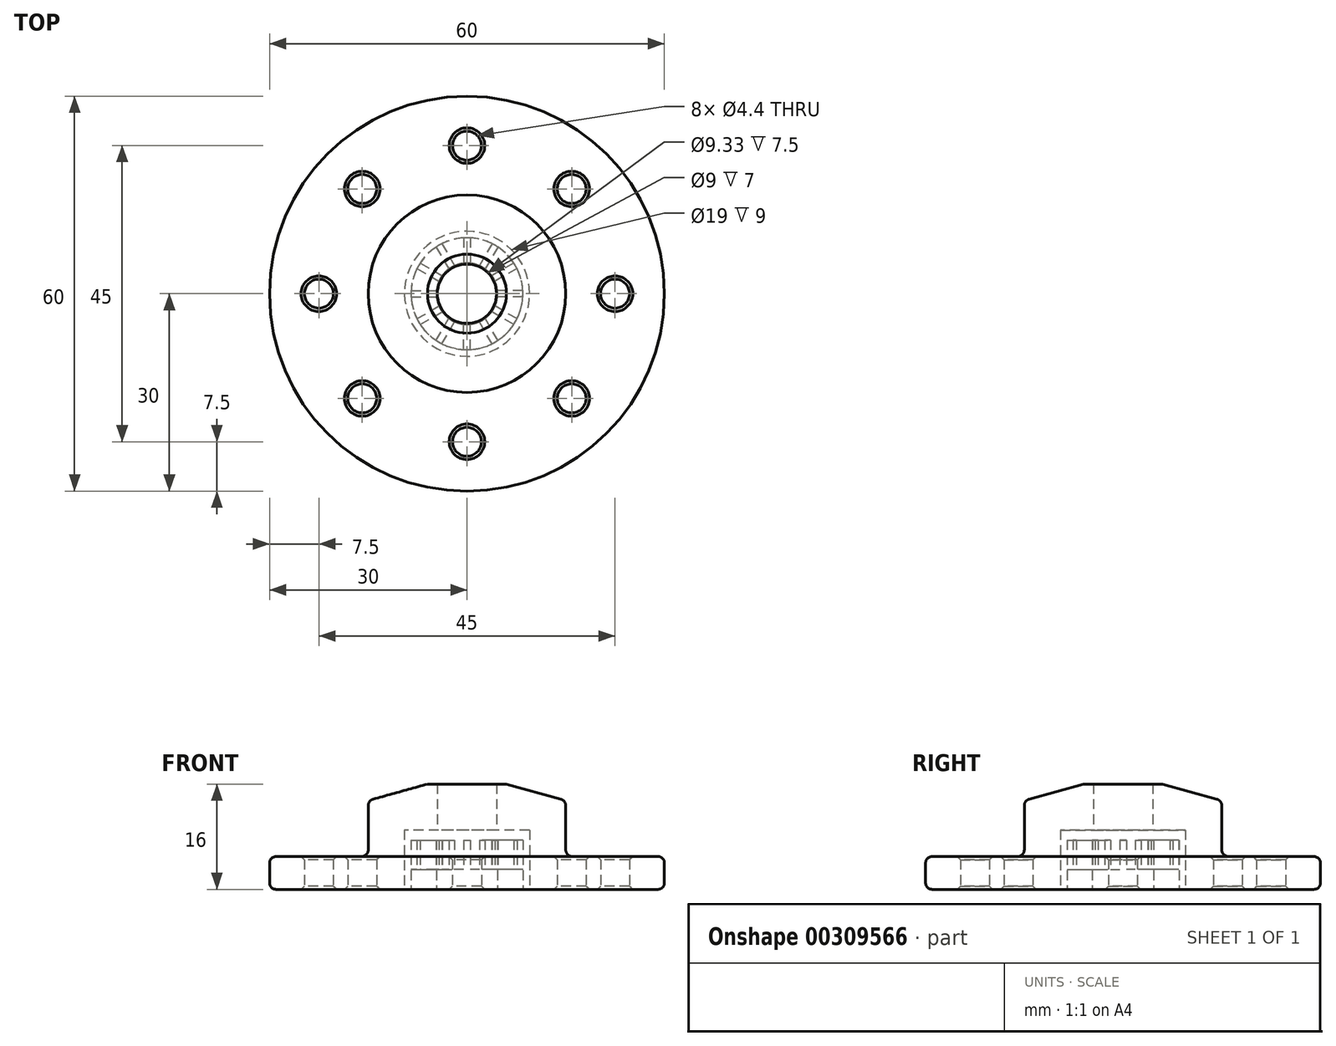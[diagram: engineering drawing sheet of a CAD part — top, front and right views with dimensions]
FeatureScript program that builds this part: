
annotation { "Feature Type Name" : "Feature", "Feature Type Description" : "" }
export const myFeature = defineFeature(function(context is Context, id is Id, definition is map)
    precondition{}
    {
        {
            var Q0;
            Q0=qCreatedBy(makeId("Top.planeOp"),FACE);
            var sketch = newSketch(context, id + "F0", { "sketchPlane" : qUnion([Q0])});
            skCircle(sketch, "E0", {"center": v(0, 0) * mm, "radius": 4.5 * mm});
            skCircle(sketch, "E1", {"center": v(0, 0) * mm, "radius": 6 * mm});
            skCircle(sketch, "E2", {"center": v(0, 0) * mm, "radius": 30 * mm});
            skCircle(sketch, "E3", {"center": v(0, 0) * mm, "radius": 9.5 * mm});
            skCircle(sketch, "E4", {"center": v(0, 0) * mm, "radius": 15 * mm});
            skLineSegment(sketch, "E5", {"start": v(15, 0) * mm, "end": v(30, 0) * mm});
            skCircle(sketch, "E6", {"center": v(22.5, 0) * mm, "radius": 2.2 * mm});
            skCircle(sketch, "E7.1.0", {"center": v(15.9, 15.9) * mm, "radius": 2.2 * mm});
            skCircle(sketch, "E7.2.0", {"center": v(0, 22.5) * mm, "radius": 2.2 * mm});
            skCircle(sketch, "E7.3.0", {"center": v(-15.9, 15.9) * mm, "radius": 2.2 * mm});
            skCircle(sketch, "E7.4.0", {"center": v(-22.5, 0) * mm, "radius": 2.2 * mm});
            skCircle(sketch, "E7.5.0", {"center": v(-15.9, -15.9) * mm, "radius": 2.2 * mm});
            skCircle(sketch, "E7.6.0", {"center": v(0, -22.5) * mm, "radius": 2.2 * mm});
            skCircle(sketch, "E7.7.0", {"center": v(15.9, -15.9) * mm, "radius": 2.2 * mm});
            skSolve(sketch);
        }
        {
            var Q0;
            Q0=makeQuery(id+"F0.imprint","IMPRINT",FACE,{"disambiguationData":[TD([[makeQuery(id+"F0.imprint","IMPRINT",EDGE,{"derivedFrom":sQuery(id+"F0.wireOp",EDGE,"E1")}),-1.0]])]});
            var Q1;
            Q1=makeQuery(id+"F0.imprint","IMPRINT",FACE,{"disambiguationData":[TD([[makeQuery(id+"F0.imprint","IMPRINT",EDGE,{"derivedFrom":sQuery(id+"F0.wireOp",EDGE,"E2")}),1.0]])]});
            var Q2;
            Q2=makeQuery(id+"F0.imprint","IMPRINT",FACE,{"disambiguationData":[TD([[makeQuery(id+"F0.imprint","IMPRINT",EDGE,{"derivedFrom":sQuery(id+"F0.wireOp",EDGE,"E3")}),-1.0]])]});
            extrude(context, id + "F1", {"entities" : qUnion([Q0, Q1, Q2]), "depth" : 5 * mm});
        }
        {
            var Q0;
            Q0=makeQuery(id+"F0.imprint","IMPRINT",FACE,{"disambiguationData":[TD([[makeQuery(id+"F0.imprint","IMPRINT",EDGE,{"derivedFrom":sQuery(id+"F0.wireOp",EDGE,"E0")}),-1.0]])]});
            extrude(context, id + "F2", {"entities" : qUnion([Q0]), "operationType" : NewBodyOperationType.ADD, "depth" : 16 * mm});
        }
        {
            var Q0;
            Q0=makeQuery(id+"F0.imprint","IMPRINT",FACE,{"disambiguationData":[TD([[makeQuery(id+"F0.imprint","IMPRINT",EDGE,{"derivedFrom":sQuery(id+"F0.wireOp",EDGE,"E3")}),-1.0]])]});
            var Q1;
            Q1=makeQuery(id+"F0.imprint","IMPRINT",FACE,{"disambiguationData":[TD([[makeQuery(id+"F0.imprint","IMPRINT",EDGE,{"derivedFrom":sQuery(id+"F0.wireOp",EDGE,"E1")}),-1.0]])]});
            extrude(context, id + "F3", {"entities" : qUnion([Q0, Q1]), "operationType" : NewBodyOperationType.ADD, "depth" : 13.5 * mm});
        }
        {
            var Q0;
            Q0=makeQuery(id+"F0.imprint","IMPRINT",FACE,{"disambiguationData":[TD([[makeQuery(id+"F0.imprint","IMPRINT",EDGE,{"derivedFrom":sQuery(id+"F0.wireOp",EDGE,"E0")}),-1.0]])]});
            var Q1;
            Q1=makeQuery(id+"F0.imprint","IMPRINT",FACE,{"disambiguationData":[TD([[makeQuery(id+"F0.imprint","IMPRINT",EDGE,{"derivedFrom":sQuery(id+"F0.wireOp",EDGE,"E1")}),-1.0]])]});
            extrude(context, id + "F4", {"entities" : qUnion([Q0, Q1]), "operationType" : NewBodyOperationType.REMOVE, "depth" : 9 * mm});
        }
        {
            var Q0;
            Q0=qCreatedBy(makeId("Front.planeOp"),FACE);
            var sketch = newSketch(context, id + "F5", { "sketchPlane" : qUnion([Q0])});
            skLineSegment(sketch, "E8", {"start": v(0, 0) * mm, "end": v(0, 16) * mm});
            skLineSegment(sketch, "E9", {"start": v(0, 16) * mm, "end": v(6, 16) * mm});
            skLineSegment(sketch, "E10", {"start": v(6, 16) * mm, "end": v(6, 13.5) * mm});
            skLineSegment(sketch, "E11", {"start": v(6, 13.5) * mm, "end": v(15, 13.5) * mm});
            skLineSegment(sketch, "E12", {"start": v(15, 13.5) * mm, "end": v(6, 16) * mm});
            skSolve(sketch);
        }
        {
            var Q0;
            Q0=makeQuery(id+"F5.imprint","IMPRINT",FACE,{"disambiguationData":[TD([[makeQuery(id+"F5.imprint","IMPRINT",EDGE,{"derivedFrom":sQuery(id+"F5.wireOp",EDGE,"E10")}),1.0]])]});
            var Q1;
            Q1=sQuery(id+"F5.wireOp",EDGE,"E8");
            revolve(context, id + "F6", {"operationType" : NewBodyOperationType.ADD, "entities" : qUnion([Q0]), "axis" : qUnion([Q1]), "revolveType" : RevolveType.FULL});
        }
        {
            var Q0;
            Q0=makeQuery(id+"F1.opExtrude","SWEPT_FACE",FACE,{"disambiguationData":[OSD([sQuery(id+"F0.wireOp",EDGE,"E2")])]});
            var Q1;
            Q1=makeQuery(id+"F3.opExtrude","SWEPT_FACE",FACE,{"disambiguationData":[OSD([sQuery(id+"F0.wireOp",EDGE,"E4")])]});
            var Q2;
            Q2=makeQuery(id+"F4.boolean.opBoolean","COPY",EDGE,{"derivedFrom":makeQuery(id+"F4.opExtrude","CAP_EDGE",EDGE,{"disambiguationData":[OSD([sQuery(id+"F0.wireOp",EDGE,"E3")])],"isStart":true})});
            fillet(context, id + "F7", {"entities" : qUnion([Q0, Q1, Q2]), "radius" : 1 * mm, "tangentPropagation" : true, "allowEdgeOverflow" : false});
        }
        {
            var Q0;
            Q0=makeQuery(id+"F1.opExtrude","SWEPT_FACE",FACE,{"disambiguationData":[OSD([sQuery(id+"F0.wireOp",EDGE,"E7.3.0")])]});
            var Q1;
            Q1=makeQuery(id+"F1.opExtrude","SWEPT_FACE",FACE,{"disambiguationData":[OSD([sQuery(id+"F0.wireOp",EDGE,"E7.2.0")])]});
            var Q2;
            Q2=makeQuery(id+"F1.opExtrude","SWEPT_FACE",FACE,{"disambiguationData":[OSD([sQuery(id+"F0.wireOp",EDGE,"E7.4.0")])]});
            var Q3;
            Q3=makeQuery(id+"F1.opExtrude","SWEPT_FACE",FACE,{"disambiguationData":[OSD([sQuery(id+"F0.wireOp",EDGE,"E7.5.0")])]});
            var Q4;
            Q4=makeQuery(id+"F1.opExtrude","SWEPT_FACE",FACE,{"disambiguationData":[OSD([sQuery(id+"F0.wireOp",EDGE,"E7.1.0")])]});
            var Q5;
            Q5=makeQuery(id+"F1.opExtrude","SWEPT_FACE",FACE,{"disambiguationData":[OSD([sQuery(id+"F0.wireOp",EDGE,"E7.6.0")])]});
            var Q6;
            Q6=makeQuery(id+"F1.opExtrude","SWEPT_FACE",FACE,{"disambiguationData":[OSD([sQuery(id+"F0.wireOp",EDGE,"E7.7.0")])]});
            var Q7;
            Q7=makeQuery(id+"F1.opExtrude","SWEPT_FACE",FACE,{"disambiguationData":[OSD([sQuery(id+"F0.wireOp",EDGE,"E6")])]});
            var Q8;
            Q8=makeQuery(id+"F4.boolean.opBoolean","COPY",EDGE,{"derivedFrom":makeQuery(id+"F4.opExtrude","CAP_EDGE",EDGE,{"disambiguationData":[OSD([sQuery(id+"F0.wireOp",EDGE,"E0")])],"isStart":false})});
            chamfer(context, id + "F8", {"entities" : qUnion([Q0, Q1, Q2, Q3, Q4, Q5, Q6, Q7, Q8]), "width" : 0.5 * mm, "tangentPropagation" : true});
        }
        {
            var Q0;
            {var subQ0=sQuery(id+"F0.wireOp",EDGE,"E1");Q0=makeQuery(id+"F2.boolean.opBoolean","MERGE",FACE,{"derivedFrom":[makeQuery(id+"F1.opExtrude","CAP_FACE",FACE,{"disambiguationData":[OSD([subQ0,sQuery(id+"F0.wireOp",EDGE,"E2"),sQuery(id+"F0.wireOp",EDGE,"E6"),sQuery(id+"F0.wireOp",EDGE,"E7.1.0"),sQuery(id+"F0.wireOp",EDGE,"E7.2.0"),sQuery(id+"F0.wireOp",EDGE,"E7.3.0"),sQuery(id+"F0.wireOp",EDGE,"E7.4.0"),sQuery(id+"F0.wireOp",EDGE,"E7.5.0"),sQuery(id+"F0.wireOp",EDGE,"E7.6.0"),sQuery(id+"F0.wireOp",EDGE,"E7.7.0")])],"isStart":true}),makeQuery(id+"F2.opExtrude","CAP_FACE",FACE,{"disambiguationData":[OSD([sQuery(id+"F0.wireOp",EDGE,"E0"),subQ0])],"isStart":true})]});}
            var sketch = newSketch(context, id + "F9", { "sketchPlane" : qUnion([Q0])});
            skCircle(sketch, "E13", {"center": v(0, 0) * mm, "radius": 4.67 * mm});
            skLineSegment(sketch, "E14", {"start": v(0, 0) * mm, "end": v(0, 4.5) * mm});
            skLineSegment(sketch, "E15", {"start": v(0, 4.5) * mm, "end": v(0, 8.5) * mm});
            skLineSegment(sketch, "E16.bottom", {"start": v(-0.5, 8.5) * mm, "end": v(0.5, 8.5) * mm});
            skLineSegment(sketch, "E16.top", {"start": v(-0.5, 4.5) * mm, "end": v(0.5, 4.5) * mm});
            skLineSegment(sketch, "E16.left", {"start": v(-0.5, 8.5) * mm, "end": v(-0.5, 4.5) * mm});
            skLineSegment(sketch, "E16.right", {"start": v(0.5, 8.5) * mm, "end": v(0.5, 4.5) * mm});
            skPoint(sketch, "E16.middle", {"position": v(0, 6.5) * mm});
            skCircle(sketch, "E17", {"center": v(0, 0) * mm, "radius": 8.5 * mm});
            skLineSegment(sketch, "E18.1.0", {"start": v(-3.82, 7.61) * mm, "end": v(-1.82, 4.15) * mm});
            skLineSegment(sketch, "E18.1.1", {"start": v(-4.68, 7.11) * mm, "end": v(-3.82, 7.61) * mm});
            skLineSegment(sketch, "E18.1.2", {"start": v(-4.68, 7.11) * mm, "end": v(-2.68, 3.65) * mm});
            skLineSegment(sketch, "E18.1.3", {"start": v(-2.68, 3.65) * mm, "end": v(-1.82, 4.15) * mm});
            skLineSegment(sketch, "E18.2.0", {"start": v(-7.11, 4.68) * mm, "end": v(-3.65, 2.68) * mm});
            skLineSegment(sketch, "E18.2.1", {"start": v(-7.61, 3.82) * mm, "end": v(-7.11, 4.68) * mm});
            skLineSegment(sketch, "E18.2.2", {"start": v(-7.61, 3.82) * mm, "end": v(-4.15, 1.82) * mm});
            skLineSegment(sketch, "E18.2.3", {"start": v(-4.15, 1.82) * mm, "end": v(-3.65, 2.68) * mm});
            skLineSegment(sketch, "E18.3.0", {"start": v(-8.5, 0.5) * mm, "end": v(-4.5, 0.5) * mm});
            skLineSegment(sketch, "E18.3.1", {"start": v(-8.5, -0.5) * mm, "end": v(-8.5, 0.5) * mm});
            skLineSegment(sketch, "E18.3.2", {"start": v(-8.5, -0.5) * mm, "end": v(-4.5, -0.5) * mm});
            skLineSegment(sketch, "E18.3.3", {"start": v(-4.5, -0.5) * mm, "end": v(-4.5, 0.5) * mm});
            skLineSegment(sketch, "E18.4.0", {"start": v(-7.61, -3.82) * mm, "end": v(-4.15, -1.82) * mm});
            skLineSegment(sketch, "E18.4.1", {"start": v(-7.11, -4.68) * mm, "end": v(-7.61, -3.82) * mm});
            skLineSegment(sketch, "E18.4.2", {"start": v(-7.11, -4.68) * mm, "end": v(-3.65, -2.68) * mm});
            skLineSegment(sketch, "E18.4.3", {"start": v(-3.65, -2.68) * mm, "end": v(-4.15, -1.82) * mm});
            skLineSegment(sketch, "E18.5.0", {"start": v(-4.68, -7.11) * mm, "end": v(-2.68, -3.65) * mm});
            skLineSegment(sketch, "E18.5.1", {"start": v(-3.82, -7.61) * mm, "end": v(-4.68, -7.11) * mm});
            skLineSegment(sketch, "E18.5.2", {"start": v(-3.82, -7.61) * mm, "end": v(-1.82, -4.15) * mm});
            skLineSegment(sketch, "E18.5.3", {"start": v(-1.82, -4.15) * mm, "end": v(-2.68, -3.65) * mm});
            skLineSegment(sketch, "E18.6.0", {"start": v(-0.5, -8.5) * mm, "end": v(-0.5, -4.5) * mm});
            skLineSegment(sketch, "E18.6.1", {"start": v(0.5, -8.5) * mm, "end": v(-0.5, -8.5) * mm});
            skLineSegment(sketch, "E18.6.2", {"start": v(0.5, -8.5) * mm, "end": v(0.5, -4.5) * mm});
            skLineSegment(sketch, "E18.6.3", {"start": v(0.5, -4.5) * mm, "end": v(-0.5, -4.5) * mm});
            skLineSegment(sketch, "E18.7.0", {"start": v(3.82, -7.61) * mm, "end": v(1.82, -4.15) * mm});
            skLineSegment(sketch, "E18.7.1", {"start": v(4.68, -7.11) * mm, "end": v(3.82, -7.61) * mm});
            skLineSegment(sketch, "E18.7.2", {"start": v(4.68, -7.11) * mm, "end": v(2.68, -3.65) * mm});
            skLineSegment(sketch, "E18.7.3", {"start": v(2.68, -3.65) * mm, "end": v(1.82, -4.15) * mm});
            skLineSegment(sketch, "E18.8.0", {"start": v(7.11, -4.68) * mm, "end": v(3.65, -2.68) * mm});
            skLineSegment(sketch, "E18.8.1", {"start": v(7.61, -3.82) * mm, "end": v(7.11, -4.68) * mm});
            skLineSegment(sketch, "E18.8.2", {"start": v(7.61, -3.82) * mm, "end": v(4.15, -1.82) * mm});
            skLineSegment(sketch, "E18.8.3", {"start": v(4.15, -1.82) * mm, "end": v(3.65, -2.68) * mm});
            skLineSegment(sketch, "E18.9.0", {"start": v(8.5, -0.5) * mm, "end": v(4.5, -0.5) * mm});
            skLineSegment(sketch, "E18.9.1", {"start": v(8.5, 0.5) * mm, "end": v(8.5, -0.5) * mm});
            skLineSegment(sketch, "E18.9.2", {"start": v(8.5, 0.5) * mm, "end": v(4.5, 0.5) * mm});
            skLineSegment(sketch, "E18.9.3", {"start": v(4.5, 0.5) * mm, "end": v(4.5, -0.5) * mm});
            skLineSegment(sketch, "E18.10.0", {"start": v(7.61, 3.82) * mm, "end": v(4.15, 1.82) * mm});
            skLineSegment(sketch, "E18.10.1", {"start": v(7.11, 4.68) * mm, "end": v(7.61, 3.82) * mm});
            skLineSegment(sketch, "E18.10.2", {"start": v(7.11, 4.68) * mm, "end": v(3.65, 2.68) * mm});
            skLineSegment(sketch, "E18.10.3", {"start": v(3.65, 2.68) * mm, "end": v(4.15, 1.82) * mm});
            skLineSegment(sketch, "E18.11.0", {"start": v(4.68, 7.11) * mm, "end": v(2.68, 3.65) * mm});
            skLineSegment(sketch, "E18.11.1", {"start": v(3.82, 7.61) * mm, "end": v(4.68, 7.11) * mm});
            skLineSegment(sketch, "E18.11.2", {"start": v(3.82, 7.61) * mm, "end": v(1.82, 4.15) * mm});
            skLineSegment(sketch, "E18.11.3", {"start": v(1.82, 4.15) * mm, "end": v(2.68, 3.65) * mm});
            skSolve(sketch);
        }
        {
            var Q0;
            {var subQ0=sQuery(id+"F9.wireOp",EDGE,"E18.10.2");var subQ1=sQuery(id+"F9.wireOp",EDGE,"E13");var subQ2=makeQuery(id+"F9.imprint","INTERSECT",VERTEX,{"derivedFrom":[subQ1,subQ0]});Q0=makeQuery(id+"F9.imprint","IMPRINT",FACE,{"disambiguationData":[TD([[makeQuery(id+"F9.imprint","IMPRINT",EDGE,{"disambiguationData":[TD([[subQ2,-1.0]])],"derivedFrom":subQ1}),-1.0]])]});}
            var Q1;
            {var subQ0=sQuery(id+"F9.wireOp",EDGE,"E18.11.0");var subQ1=sQuery(id+"F9.wireOp",EDGE,"E13");var subQ2=makeQuery(id+"F9.imprint","INTERSECT",VERTEX,{"derivedFrom":[subQ1,subQ0]});Q1=makeQuery(id+"F9.imprint","IMPRINT",FACE,{"disambiguationData":[TD([[makeQuery(id+"F9.imprint","IMPRINT",EDGE,{"disambiguationData":[TD([[subQ2,-1.0]])],"derivedFrom":subQ1}),-1.0]])]});}
            var Q2;
            {var subQ0=sQuery(id+"F9.wireOp",EDGE,"E18.11.2");var subQ1=sQuery(id+"F9.wireOp",EDGE,"E13");var subQ2=makeQuery(id+"F9.imprint","INTERSECT",VERTEX,{"derivedFrom":[subQ1,subQ0]});Q2=makeQuery(id+"F9.imprint","IMPRINT",FACE,{"disambiguationData":[TD([[makeQuery(id+"F9.imprint","IMPRINT",EDGE,{"disambiguationData":[TD([[subQ2,-1.0]])],"derivedFrom":subQ1}),-1.0]])]});}
            var Q3;
            {var subQ0=sQuery(id+"F9.wireOp",EDGE,"E16.right");var subQ1=sQuery(id+"F9.wireOp",EDGE,"E13");var subQ2=makeQuery(id+"F9.imprint","INTERSECT",VERTEX,{"derivedFrom":[subQ1,subQ0]});Q3=makeQuery(id+"F9.imprint","IMPRINT",FACE,{"disambiguationData":[TD([[makeQuery(id+"F9.imprint","IMPRINT",EDGE,{"disambiguationData":[TD([[subQ2,-1.0]])],"derivedFrom":subQ1}),-1.0]])]});}
            var Q4;
            {var subQ0=sQuery(id+"F9.wireOp",EDGE,"E15");var subQ1=sQuery(id+"F9.wireOp",EDGE,"E13");var subQ2=makeQuery(id+"F9.imprint","INTERSECT",VERTEX,{"derivedFrom":[subQ1,subQ0]});Q4=makeQuery(id+"F9.imprint","IMPRINT",FACE,{"disambiguationData":[TD([[makeQuery(id+"F9.imprint","IMPRINT",EDGE,{"disambiguationData":[TD([[subQ2,-1.0]])],"derivedFrom":subQ1}),-1.0]])]});}
            var Q5;
            {var subQ0=sQuery(id+"F9.wireOp",EDGE,"E16.left");var subQ1=sQuery(id+"F9.wireOp",EDGE,"E13");var subQ2=makeQuery(id+"F9.imprint","INTERSECT",VERTEX,{"derivedFrom":[subQ1,subQ0]});Q5=makeQuery(id+"F9.imprint","IMPRINT",FACE,{"disambiguationData":[TD([[makeQuery(id+"F9.imprint","IMPRINT",EDGE,{"disambiguationData":[TD([[subQ2,-1.0]])],"derivedFrom":subQ1}),-1.0]])]});}
            var Q6;
            {var subQ0=sQuery(id+"F9.wireOp",EDGE,"E18.1.0");var subQ1=sQuery(id+"F9.wireOp",EDGE,"E13");var subQ2=makeQuery(id+"F9.imprint","INTERSECT",VERTEX,{"derivedFrom":[subQ1,subQ0]});Q6=makeQuery(id+"F9.imprint","IMPRINT",FACE,{"disambiguationData":[TD([[makeQuery(id+"F9.imprint","IMPRINT",EDGE,{"disambiguationData":[TD([[subQ2,-1.0]])],"derivedFrom":subQ1}),-1.0]])]});}
            var Q7;
            {var subQ0=sQuery(id+"F9.wireOp",EDGE,"E18.1.2");var subQ1=sQuery(id+"F9.wireOp",EDGE,"E13");var subQ2=makeQuery(id+"F9.imprint","INTERSECT",VERTEX,{"derivedFrom":[subQ1,subQ0]});Q7=makeQuery(id+"F9.imprint","IMPRINT",FACE,{"disambiguationData":[TD([[makeQuery(id+"F9.imprint","IMPRINT",EDGE,{"disambiguationData":[TD([[subQ2,-1.0]])],"derivedFrom":subQ1}),-1.0]])]});}
            var Q8;
            {var subQ0=sQuery(id+"F9.wireOp",EDGE,"E18.2.0");var subQ1=sQuery(id+"F9.wireOp",EDGE,"E13");var subQ2=makeQuery(id+"F9.imprint","INTERSECT",VERTEX,{"derivedFrom":[subQ1,subQ0]});Q8=makeQuery(id+"F9.imprint","IMPRINT",FACE,{"disambiguationData":[TD([[makeQuery(id+"F9.imprint","IMPRINT",EDGE,{"disambiguationData":[TD([[subQ2,-1.0]])],"derivedFrom":subQ1}),-1.0]])]});}
            var Q9;
            {var subQ0=sQuery(id+"F9.wireOp",EDGE,"E18.2.2");var subQ1=sQuery(id+"F9.wireOp",EDGE,"E13");var subQ2=makeQuery(id+"F9.imprint","INTERSECT",VERTEX,{"derivedFrom":[subQ1,subQ0]});Q9=makeQuery(id+"F9.imprint","IMPRINT",FACE,{"disambiguationData":[TD([[makeQuery(id+"F9.imprint","IMPRINT",EDGE,{"disambiguationData":[TD([[subQ2,-1.0]])],"derivedFrom":subQ1}),-1.0]])]});}
            var Q10;
            {var subQ4=sQuery(id+"F9.wireOp",EDGE,"E18.3.0");var subQ6=sQuery(id+"F9.wireOp",EDGE,"E13");var subQ7=makeQuery(id+"F9.imprint","INTERSECT",VERTEX,{"derivedFrom":[subQ6,subQ4]});Q10=makeQuery(id+"F9.imprint","IMPRINT",FACE,{"disambiguationData":[TD([[makeQuery(id+"F9.imprint","IMPRINT",EDGE,{"disambiguationData":[TD([[subQ7,-1.0]])],"derivedFrom":subQ6}),-1.0]])]});}
            var Q11;
            {var subQ0=sQuery(id+"F9.wireOp",EDGE,"E18.3.2");var subQ1=sQuery(id+"F9.wireOp",EDGE,"E13");var subQ2=makeQuery(id+"F9.imprint","INTERSECT",VERTEX,{"derivedFrom":[subQ1,subQ0]});Q11=makeQuery(id+"F9.imprint","IMPRINT",FACE,{"disambiguationData":[TD([[makeQuery(id+"F9.imprint","IMPRINT",EDGE,{"disambiguationData":[TD([[subQ2,-1.0]])],"derivedFrom":subQ1}),-1.0]])]});}
            var Q12;
            {var subQ0=sQuery(id+"F9.wireOp",EDGE,"E18.4.0");var subQ1=sQuery(id+"F9.wireOp",EDGE,"E13");var subQ2=makeQuery(id+"F9.imprint","INTERSECT",VERTEX,{"derivedFrom":[subQ1,subQ0]});Q12=makeQuery(id+"F9.imprint","IMPRINT",FACE,{"disambiguationData":[TD([[makeQuery(id+"F9.imprint","IMPRINT",EDGE,{"disambiguationData":[TD([[subQ2,-1.0]])],"derivedFrom":subQ1}),-1.0]])]});}
            var Q13;
            {var subQ0=sQuery(id+"F9.wireOp",EDGE,"E18.4.2");var subQ1=sQuery(id+"F9.wireOp",EDGE,"E13");var subQ2=makeQuery(id+"F9.imprint","INTERSECT",VERTEX,{"derivedFrom":[subQ1,subQ0]});Q13=makeQuery(id+"F9.imprint","IMPRINT",FACE,{"disambiguationData":[TD([[makeQuery(id+"F9.imprint","IMPRINT",EDGE,{"disambiguationData":[TD([[subQ2,-1.0]])],"derivedFrom":subQ1}),-1.0]])]});}
            var Q14;
            {var subQ0=sQuery(id+"F9.wireOp",EDGE,"E18.5.0");var subQ1=sQuery(id+"F9.wireOp",EDGE,"E13");var subQ2=makeQuery(id+"F9.imprint","INTERSECT",VERTEX,{"derivedFrom":[subQ1,subQ0]});Q14=makeQuery(id+"F9.imprint","IMPRINT",FACE,{"disambiguationData":[TD([[makeQuery(id+"F9.imprint","IMPRINT",EDGE,{"disambiguationData":[TD([[subQ2,-1.0]])],"derivedFrom":subQ1}),-1.0]])]});}
            var Q15;
            {var subQ0=sQuery(id+"F9.wireOp",EDGE,"E18.5.2");var subQ1=sQuery(id+"F9.wireOp",EDGE,"E13");var subQ2=makeQuery(id+"F9.imprint","INTERSECT",VERTEX,{"derivedFrom":[subQ1,subQ0]});Q15=makeQuery(id+"F9.imprint","IMPRINT",FACE,{"disambiguationData":[TD([[makeQuery(id+"F9.imprint","IMPRINT",EDGE,{"disambiguationData":[TD([[subQ2,-1.0]])],"derivedFrom":subQ1}),-1.0]])]});}
            var Q16;
            {var subQ0=sQuery(id+"F9.wireOp",EDGE,"E18.6.0");var subQ1=sQuery(id+"F9.wireOp",EDGE,"E13");var subQ2=makeQuery(id+"F9.imprint","INTERSECT",VERTEX,{"derivedFrom":[subQ1,subQ0]});Q16=makeQuery(id+"F9.imprint","IMPRINT",FACE,{"disambiguationData":[TD([[makeQuery(id+"F9.imprint","IMPRINT",EDGE,{"disambiguationData":[TD([[subQ2,-1.0]])],"derivedFrom":subQ1}),-1.0]])]});}
            var Q17;
            {var subQ0=sQuery(id+"F9.wireOp",EDGE,"E18.6.2");var subQ1=sQuery(id+"F9.wireOp",EDGE,"E13");var subQ2=makeQuery(id+"F9.imprint","INTERSECT",VERTEX,{"derivedFrom":[subQ1,subQ0]});Q17=makeQuery(id+"F9.imprint","IMPRINT",FACE,{"disambiguationData":[TD([[makeQuery(id+"F9.imprint","IMPRINT",EDGE,{"disambiguationData":[TD([[subQ2,-1.0]])],"derivedFrom":subQ1}),-1.0]])]});}
            var Q18;
            {var subQ0=sQuery(id+"F9.wireOp",EDGE,"E18.7.0");var subQ1=sQuery(id+"F9.wireOp",EDGE,"E13");var subQ2=makeQuery(id+"F9.imprint","INTERSECT",VERTEX,{"derivedFrom":[subQ1,subQ0]});Q18=makeQuery(id+"F9.imprint","IMPRINT",FACE,{"disambiguationData":[TD([[makeQuery(id+"F9.imprint","IMPRINT",EDGE,{"disambiguationData":[TD([[subQ2,-1.0]])],"derivedFrom":subQ1}),-1.0]])]});}
            var Q19;
            {var subQ0=sQuery(id+"F9.wireOp",EDGE,"E18.7.2");var subQ1=sQuery(id+"F9.wireOp",EDGE,"E13");var subQ2=makeQuery(id+"F9.imprint","INTERSECT",VERTEX,{"derivedFrom":[subQ1,subQ0]});Q19=makeQuery(id+"F9.imprint","IMPRINT",FACE,{"disambiguationData":[TD([[makeQuery(id+"F9.imprint","IMPRINT",EDGE,{"disambiguationData":[TD([[subQ2,-1.0]])],"derivedFrom":subQ1}),-1.0]])]});}
            var Q20;
            {var subQ4=sQuery(id+"F9.wireOp",EDGE,"E18.8.0");var subQ6=sQuery(id+"F9.wireOp",EDGE,"E13");var subQ7=makeQuery(id+"F9.imprint","INTERSECT",VERTEX,{"derivedFrom":[subQ6,subQ4]});Q20=makeQuery(id+"F9.imprint","IMPRINT",FACE,{"disambiguationData":[TD([[makeQuery(id+"F9.imprint","IMPRINT",EDGE,{"disambiguationData":[TD([[subQ7,-1.0]])],"derivedFrom":subQ6}),-1.0]])]});}
            var Q21;
            {var subQ0=sQuery(id+"F9.wireOp",EDGE,"E18.8.2");var subQ1=sQuery(id+"F9.wireOp",EDGE,"E13");var subQ2=makeQuery(id+"F9.imprint","INTERSECT",VERTEX,{"derivedFrom":[subQ1,subQ0]});Q21=makeQuery(id+"F9.imprint","IMPRINT",FACE,{"disambiguationData":[TD([[makeQuery(id+"F9.imprint","IMPRINT",EDGE,{"disambiguationData":[TD([[subQ2,-1.0]])],"derivedFrom":subQ1}),-1.0]])]});}
            var Q22;
            {var subQ1=sQuery(id+"F9.wireOp",EDGE,"E13");var subQ6=sQuery(id+"F9.wireOp",EDGE,"E18.9.2");var subQ8=makeQuery(id+"F9.imprint","INTERSECT",VERTEX,{"derivedFrom":[subQ1,subQ6]});Q22=makeQuery(id+"F9.imprint","IMPRINT",FACE,{"disambiguationData":[TD([[makeQuery(id+"F9.imprint","IMPRINT",EDGE,{"disambiguationData":[TD([[subQ8,1.0]])],"derivedFrom":subQ1}),-1.0]])]});}
            var Q23;
            {var subQ0=sQuery(id+"F9.wireOp",EDGE,"E18.10.0");var subQ1=sQuery(id+"F9.wireOp",EDGE,"E13");var subQ2=makeQuery(id+"F9.imprint","INTERSECT",VERTEX,{"derivedFrom":[subQ1,subQ0]});Q23=makeQuery(id+"F9.imprint","IMPRINT",FACE,{"disambiguationData":[TD([[makeQuery(id+"F9.imprint","IMPRINT",EDGE,{"disambiguationData":[TD([[subQ2,1.0]])],"derivedFrom":subQ1}),-1.0]])]});}
            var Q24;
            {var subQ0=sQuery(id+"F9.wireOp",EDGE,"E18.10.0");var subQ1=sQuery(id+"F9.wireOp",EDGE,"E13");var subQ2=makeQuery(id+"F9.imprint","INTERSECT",VERTEX,{"derivedFrom":[subQ1,subQ0]});Q24=makeQuery(id+"F9.imprint","IMPRINT",FACE,{"disambiguationData":[TD([[makeQuery(id+"F9.imprint","IMPRINT",EDGE,{"disambiguationData":[TD([[subQ2,-1.0]])],"derivedFrom":subQ1}),-1.0]])]});}
            extrude(context, id + "F10", {"entities" : qUnion([Q0, Q1, Q2, Q3, Q4, Q5, Q6, Q7, Q8, Q9, Q10, Q11, Q12, Q13, Q14, Q15, Q16, Q17, Q18, Q19, Q20, Q21, Q22, Q23, Q24]), "oppositeDirection" : true, "depth" : 3 * mm});
        }
        {
            var Q0;
            {var subQ4=sQuery(id+"F9.wireOp",EDGE,"E18.3.0");var subQ6=sQuery(id+"F9.wireOp",EDGE,"E13");var subQ7=makeQuery(id+"F9.imprint","INTERSECT",VERTEX,{"derivedFrom":[subQ6,subQ4]});Q0=makeQuery(id+"F9.imprint","IMPRINT",FACE,{"disambiguationData":[TD([[makeQuery(id+"F9.imprint","IMPRINT",EDGE,{"disambiguationData":[TD([[subQ7,-1.0]])],"derivedFrom":subQ6}),-1.0]])]});}
            var Q1;
            {var subQ0=sQuery(id+"F9.wireOp",EDGE,"E18.2.0");var subQ1=sQuery(id+"F9.wireOp",EDGE,"E13");var subQ2=makeQuery(id+"F9.imprint","INTERSECT",VERTEX,{"derivedFrom":[subQ1,subQ0]});Q1=makeQuery(id+"F9.imprint","IMPRINT",FACE,{"disambiguationData":[TD([[makeQuery(id+"F9.imprint","IMPRINT",EDGE,{"disambiguationData":[TD([[subQ2,-1.0]])],"derivedFrom":subQ1}),-1.0]])]});}
            var Q2;
            {var subQ0=sQuery(id+"F9.wireOp",EDGE,"E18.1.0");var subQ1=sQuery(id+"F9.wireOp",EDGE,"E13");var subQ2=makeQuery(id+"F9.imprint","INTERSECT",VERTEX,{"derivedFrom":[subQ1,subQ0]});Q2=makeQuery(id+"F9.imprint","IMPRINT",FACE,{"disambiguationData":[TD([[makeQuery(id+"F9.imprint","IMPRINT",EDGE,{"disambiguationData":[TD([[subQ2,-1.0]])],"derivedFrom":subQ1}),-1.0]])]});}
            var Q3;
            {var subQ0=sQuery(id+"F9.wireOp",EDGE,"E15");var subQ1=sQuery(id+"F9.wireOp",EDGE,"E13");var subQ2=makeQuery(id+"F9.imprint","INTERSECT",VERTEX,{"derivedFrom":[subQ1,subQ0]});Q3=makeQuery(id+"F9.imprint","IMPRINT",FACE,{"disambiguationData":[TD([[makeQuery(id+"F9.imprint","IMPRINT",EDGE,{"disambiguationData":[TD([[subQ2,-1.0]])],"derivedFrom":subQ1}),-1.0]])]});}
            var Q4;
            {var subQ0=sQuery(id+"F9.wireOp",EDGE,"E16.right");var subQ1=sQuery(id+"F9.wireOp",EDGE,"E13");var subQ2=makeQuery(id+"F9.imprint","INTERSECT",VERTEX,{"derivedFrom":[subQ1,subQ0]});Q4=makeQuery(id+"F9.imprint","IMPRINT",FACE,{"disambiguationData":[TD([[makeQuery(id+"F9.imprint","IMPRINT",EDGE,{"disambiguationData":[TD([[subQ2,-1.0]])],"derivedFrom":subQ1}),-1.0]])]});}
            var Q5;
            {var subQ0=sQuery(id+"F9.wireOp",EDGE,"E18.11.0");var subQ1=sQuery(id+"F9.wireOp",EDGE,"E13");var subQ2=makeQuery(id+"F9.imprint","INTERSECT",VERTEX,{"derivedFrom":[subQ1,subQ0]});Q5=makeQuery(id+"F9.imprint","IMPRINT",FACE,{"disambiguationData":[TD([[makeQuery(id+"F9.imprint","IMPRINT",EDGE,{"disambiguationData":[TD([[subQ2,-1.0]])],"derivedFrom":subQ1}),-1.0]])]});}
            var Q6;
            {var subQ0=sQuery(id+"F9.wireOp",EDGE,"E18.10.0");var subQ1=sQuery(id+"F9.wireOp",EDGE,"E13");var subQ2=makeQuery(id+"F9.imprint","INTERSECT",VERTEX,{"derivedFrom":[subQ1,subQ0]});Q6=makeQuery(id+"F9.imprint","IMPRINT",FACE,{"disambiguationData":[TD([[makeQuery(id+"F9.imprint","IMPRINT",EDGE,{"disambiguationData":[TD([[subQ2,-1.0]])],"derivedFrom":subQ1}),-1.0]])]});}
            var Q7;
            {var subQ1=sQuery(id+"F9.wireOp",EDGE,"E13");var subQ6=sQuery(id+"F9.wireOp",EDGE,"E18.9.2");var subQ8=makeQuery(id+"F9.imprint","INTERSECT",VERTEX,{"derivedFrom":[subQ1,subQ6]});Q7=makeQuery(id+"F9.imprint","IMPRINT",FACE,{"disambiguationData":[TD([[makeQuery(id+"F9.imprint","IMPRINT",EDGE,{"disambiguationData":[TD([[subQ8,1.0]])],"derivedFrom":subQ1}),-1.0]])]});}
            var Q8;
            {var subQ4=sQuery(id+"F9.wireOp",EDGE,"E18.8.0");var subQ6=sQuery(id+"F9.wireOp",EDGE,"E13");var subQ7=makeQuery(id+"F9.imprint","INTERSECT",VERTEX,{"derivedFrom":[subQ6,subQ4]});Q8=makeQuery(id+"F9.imprint","IMPRINT",FACE,{"disambiguationData":[TD([[makeQuery(id+"F9.imprint","IMPRINT",EDGE,{"disambiguationData":[TD([[subQ7,-1.0]])],"derivedFrom":subQ6}),-1.0]])]});}
            var Q9;
            {var subQ0=sQuery(id+"F9.wireOp",EDGE,"E18.7.0");var subQ1=sQuery(id+"F9.wireOp",EDGE,"E13");var subQ2=makeQuery(id+"F9.imprint","INTERSECT",VERTEX,{"derivedFrom":[subQ1,subQ0]});Q9=makeQuery(id+"F9.imprint","IMPRINT",FACE,{"disambiguationData":[TD([[makeQuery(id+"F9.imprint","IMPRINT",EDGE,{"disambiguationData":[TD([[subQ2,-1.0]])],"derivedFrom":subQ1}),-1.0]])]});}
            var Q10;
            {var subQ0=sQuery(id+"F9.wireOp",EDGE,"E18.6.0");var subQ1=sQuery(id+"F9.wireOp",EDGE,"E13");var subQ2=makeQuery(id+"F9.imprint","INTERSECT",VERTEX,{"derivedFrom":[subQ1,subQ0]});Q10=makeQuery(id+"F9.imprint","IMPRINT",FACE,{"disambiguationData":[TD([[makeQuery(id+"F9.imprint","IMPRINT",EDGE,{"disambiguationData":[TD([[subQ2,-1.0]])],"derivedFrom":subQ1}),-1.0]])]});}
            var Q11;
            {var subQ0=sQuery(id+"F9.wireOp",EDGE,"E18.5.0");var subQ1=sQuery(id+"F9.wireOp",EDGE,"E13");var subQ2=makeQuery(id+"F9.imprint","INTERSECT",VERTEX,{"derivedFrom":[subQ1,subQ0]});Q11=makeQuery(id+"F9.imprint","IMPRINT",FACE,{"disambiguationData":[TD([[makeQuery(id+"F9.imprint","IMPRINT",EDGE,{"disambiguationData":[TD([[subQ2,-1.0]])],"derivedFrom":subQ1}),-1.0]])]});}
            var Q12;
            {var subQ0=sQuery(id+"F9.wireOp",EDGE,"E18.4.0");var subQ1=sQuery(id+"F9.wireOp",EDGE,"E13");var subQ2=makeQuery(id+"F9.imprint","INTERSECT",VERTEX,{"derivedFrom":[subQ1,subQ0]});Q12=makeQuery(id+"F9.imprint","IMPRINT",FACE,{"disambiguationData":[TD([[makeQuery(id+"F9.imprint","IMPRINT",EDGE,{"disambiguationData":[TD([[subQ2,-1.0]])],"derivedFrom":subQ1}),-1.0]])]});}
            extrude(context, id + "F11", {"entities" : qUnion([Q0, Q1, Q2, Q3, Q4, Q5, Q6, Q7, Q8, Q9, Q10, Q11, Q12]), "operationType" : NewBodyOperationType.ADD, "oppositeDirection" : true, "depth" : 7.5 * mm});
        }
    });
